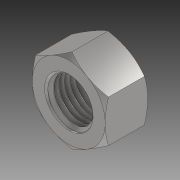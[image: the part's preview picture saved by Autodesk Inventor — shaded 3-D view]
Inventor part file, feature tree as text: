
AUTODESK INVENTOR PART (.ipt)
format: ipt  version: 2020 (Build 240168000, 168)  size: 369,152 bytes
history: mixed  units: in
note: dims shown in document units (in); Inventor stores cm internally (conversion verified against a paired STEP export)
features: other x1, sketch x1, mirror x1, imported_body x1
ambient origin geometry x8: Origin, YZ Plane, XZ Plane, XY Plane, X Axis, Y Axis, Z Axis, Center Point
bodies: Solid1 (imported_parasolid)
feature tree (4):
  other  "Repaired Geometry1"
  sketch  "3D Sketch1"
  mirror  "Mirror1"
  imported_body  NMx_Import_Brep_tag  [imported B-rep: ~8 faces, bbox_mm=[3.571875, 6.186669, 0.0]]
